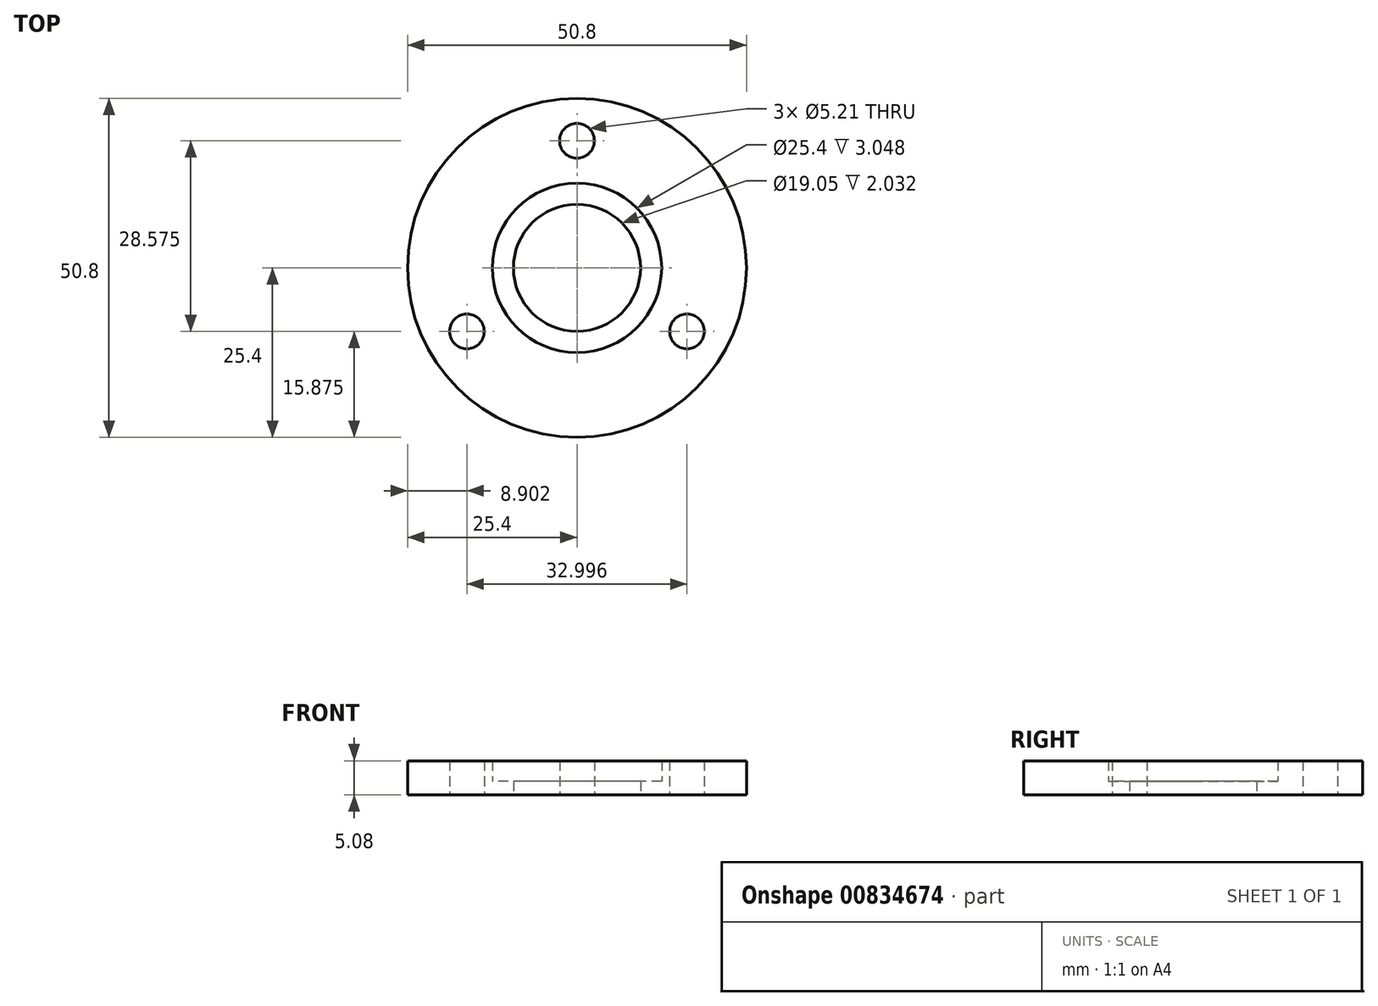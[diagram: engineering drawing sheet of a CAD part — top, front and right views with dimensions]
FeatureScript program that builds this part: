
annotation { "Feature Type Name" : "Feature", "Feature Type Description" : "" }
export const myFeature = defineFeature(function(context is Context, id is Id, definition is map)
    precondition{}
    {
        {
            var Q0;
            Q0=qCreatedBy(makeId("Top.planeOp"),FACE);
            var sketch = newSketch(context, id + "F0", { "sketchPlane" : qUnion([Q0])});
            skCircle(sketch, "E0", {"center": v(0, 0) * mm, "radius": 9.53 * mm});
            skCircle(sketch, "E1", {"center": v(0, 0) * mm, "radius": 12.7 * mm});
            skCircle(sketch, "E2", {"center": v(0, 0) * mm, "radius": 25.4 * mm});
            skCircle(sketch, "E3", {"center": v(0, 19.05) * mm, "radius": 2.6 * mm});
            skCircle(sketch, "E4.1.0", {"center": v(-16.5, -9.52) * mm, "radius": 2.6 * mm});
            skCircle(sketch, "E4.2.0", {"center": v(16.5, -9.53) * mm, "radius": 2.6 * mm});
            skSolve(sketch);
        }
        {
            var Q0;
            Q0=makeQuery(id+"F0.imprint","IMPRINT",FACE,{"disambiguationData":[TD([[makeQuery(id+"F0.imprint","IMPRINT",EDGE,{"derivedFrom":sQuery(id+"F0.wireOp",EDGE,"E1")}),-1.0]])]});
            extrude(context, id + "F1", {"entities" : qUnion([Q0]), "depth" : 5.08 * mm, "offsetDistance" : 25.4 * mm});
        }
        {
            var Q0;
            Q0=makeQuery(id+"F0.imprint","IMPRINT",FACE,{"disambiguationData":[TD([[makeQuery(id+"F0.imprint","IMPRINT",EDGE,{"derivedFrom":sQuery(id+"F0.wireOp",EDGE,"E0")}),-1.0]])]});
            extrude(context, id + "F2", {"entities" : qUnion([Q0]), "operationType" : NewBodyOperationType.ADD, "depth" : 2.03 * mm, "offsetDistance" : 25.4 * mm});
        }
    });
